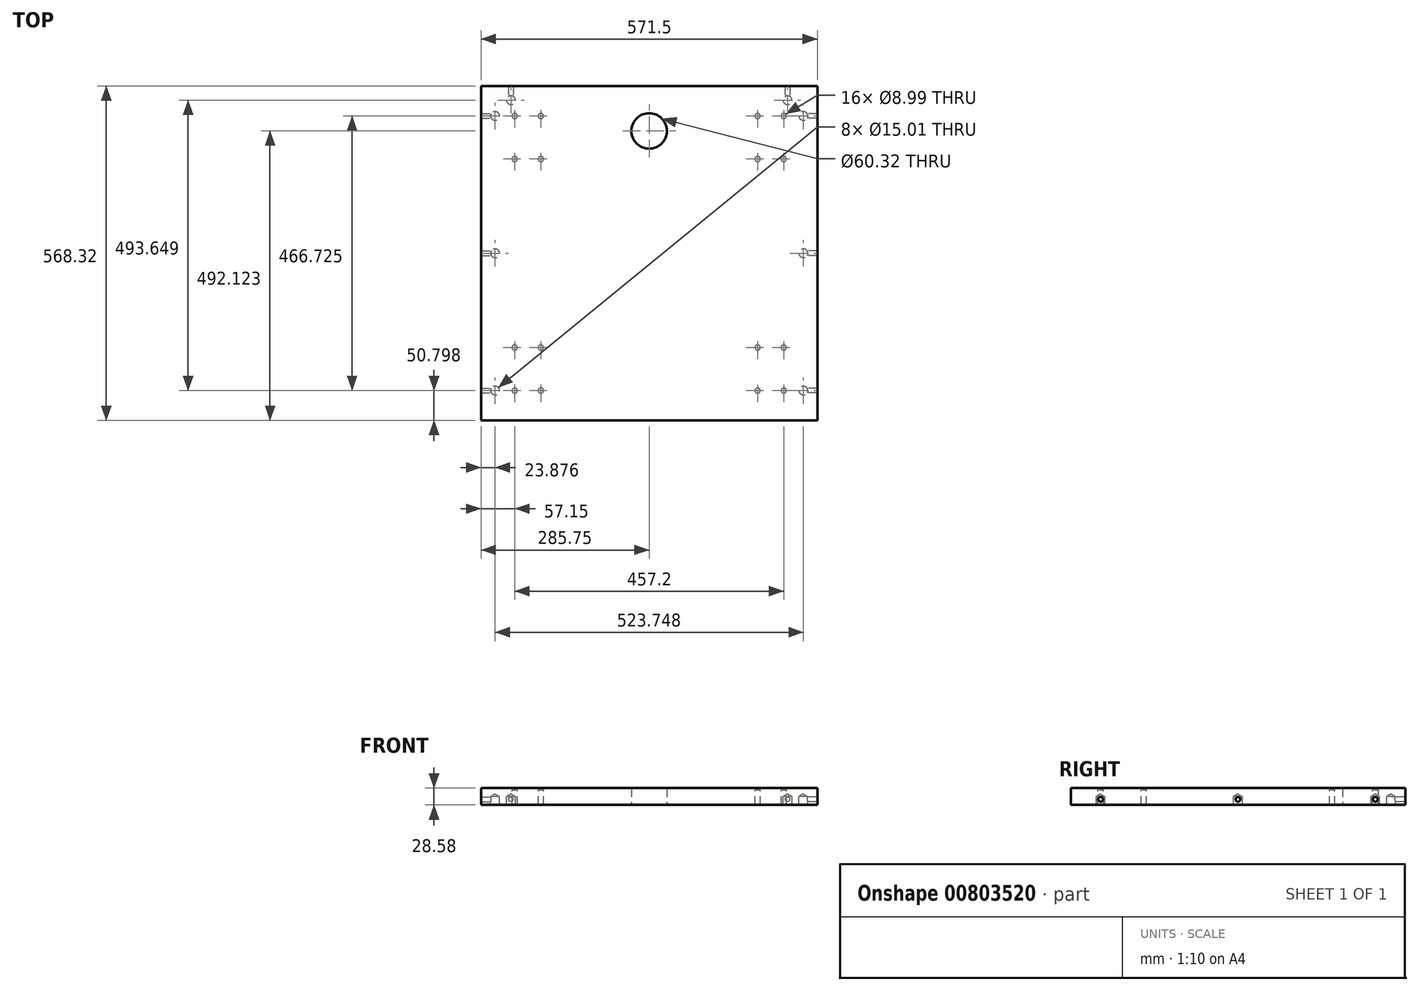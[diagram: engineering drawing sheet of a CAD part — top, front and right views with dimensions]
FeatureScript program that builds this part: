
annotation { "Feature Type Name" : "Feature", "Feature Type Description" : "" }
export const myFeature = defineFeature(function(context is Context, id is Id, definition is map)
    precondition{}
    {
        {
            var Q0;
            Q0=qCreatedBy(makeId("Top.planeOp"),FACE);
            var sketch = newSketch(context, id + "F0", { "sketchPlane" : qUnion([Q0])});
            skLineSegment(sketch, "E0.bottom", {"start": v(285.75, 284.16) * mm, "end": v(-285.75, 284.16) * mm});
            skLineSegment(sketch, "E0.top", {"start": v(285.75, -284.16) * mm, "end": v(-285.75, -284.16) * mm});
            skLineSegment(sketch, "E0.left", {"start": v(285.75, 284.16) * mm, "end": v(285.75, -284.16) * mm});
            skLineSegment(sketch, "E0.right", {"start": v(-285.75, 284.16) * mm, "end": v(-285.75, -284.16) * mm});
            skPoint(sketch, "E0.middle", {"position": v(0, 0) * mm});
            skLineSegment(sketch, "E1", {"start": v(0, 284.16) * mm, "end": v(0, 207.96) * mm});
            skCircle(sketch, "E2", {"center": v(0, 207.96) * mm, "radius": 30.16 * mm});
            skSolve(sketch);
        }
        {
            var Q0;
            Q0=makeQuery(id+"F0.imprint","IMPRINT",FACE,{"disambiguationData":[TD([[makeQuery(id+"F0.imprint","IMPRINT",EDGE,{"derivedFrom":sQuery(id+"F0.wireOp",EDGE,"E0.top")}),-1.0]])]});
            extrude(context, id + "F1", {"entities" : qUnion([Q0]), "depth" : 28.57 * mm, "offsetDistance" : 25.4 * mm});
        }
        {
            var Q0;
            Q0=makeQuery(id+"F1.opExtrude","CAP_FACE",FACE,{"disambiguationData":[OSD([sQuery(id+"F0.wireOp",EDGE,"E0.bottom"),sQuery(id+"F0.wireOp",EDGE,"E0.top"),sQuery(id+"F0.wireOp",EDGE,"E0.left"),sQuery(id+"F0.wireOp",EDGE,"E0.right"),sQuery(id+"F0.wireOp",EDGE,"E2")])],"isStart":true});
            var sketch = newSketch(context, id + "F2", { "sketchPlane" : qUnion([Q0])});
            skLineSegment(sketch, "E3", {"start": v(-285.75, 284.16) * mm, "end": v(-261.87, 284.16) * mm});
            skLineSegment(sketch, "E4", {"start": v(-261.87, 284.16) * mm, "end": v(-261.87, 233.36) * mm});
            skLineSegment(sketch, "E5", {"start": v(-285.75, -284.16) * mm, "end": v(-261.87, -284.16) * mm});
            skLineSegment(sketch, "E6", {"start": v(-261.87, -284.16) * mm, "end": v(-261.87, -233.36) * mm});
            skLineSegment(sketch, "E7", {"start": v(-285.75, 0) * mm, "end": v(-261.87, 0) * mm});
            skLineSegment(sketch, "E8", {"start": v(285.75, 0) * mm, "end": v(261.87, 0) * mm});
            skLineSegment(sketch, "E9", {"start": v(285.75, 284.16) * mm, "end": v(261.87, 284.16) * mm});
            skLineSegment(sketch, "E10", {"start": v(261.87, 284.16) * mm, "end": v(261.87, 233.36) * mm});
            skLineSegment(sketch, "E11", {"start": v(285.75, -284.16) * mm, "end": v(261.87, -284.16) * mm});
            skLineSegment(sketch, "E12", {"start": v(261.87, -284.16) * mm, "end": v(261.87, -233.36) * mm});
            skPoint(sketch, "E13", {"position": v(-261.87, 233.36) * mm});
            skPoint(sketch, "E14", {"position": v(-261.87, 0) * mm});
            skPoint(sketch, "E15", {"position": v(-261.87, -233.36) * mm});
            skPoint(sketch, "E16", {"position": v(261.87, -233.36) * mm});
            skPoint(sketch, "E17", {"position": v(261.87, 0) * mm});
            skPoint(sketch, "E18", {"position": v(261.87, 233.36) * mm});
            skSolve(sketch);
        }
        {
            var Q0;
            Q0=sQuery(id+"F2.wireOp",VERTEX,"E13");
            var Q1;
            Q1=sQuery(id+"F2.wireOp",VERTEX,"E18");
            var Q2;
            Q2=sQuery(id+"F2.wireOp",VERTEX,"E14");
            var Q3;
            Q3=sQuery(id+"F2.wireOp",VERTEX,"E17");
            var Q4;
            Q4=sQuery(id+"F2.wireOp",VERTEX,"E16");
            var Q5;
            Q5=sQuery(id+"F2.wireOp",VERTEX,"E15");
            var Q6;
            Q6=makeQuery(id+"F1.opExtrude","SWEPT_BODY",BODY,{"disambiguationData":[OSD([sQuery(id+"F0.wireOp",EDGE,"E0.bottom"),sQuery(id+"F0.wireOp",EDGE,"E0.top"),sQuery(id+"F0.wireOp",EDGE,"E0.left"),sQuery(id+"F0.wireOp",EDGE,"E0.right"),sQuery(id+"F0.wireOp",EDGE,"E2")])]});
            hole(context, id + "F3", {"style" : HoleStyle.SIMPLE, "endStyle" : HoleEndStyle.BLIND, "holeDiameter" : 15 * mm, "majorDiameter" : 6.35 * mm, "holeDepth" : 14.22 * mm, "isTappedThrough" : true, "tappedDepth" : 12.7 * mm, "tapClearance" : 3, "startFromSketch" : true, "locations" : qUnion([Q0, Q1, Q2, Q3, Q4, Q5]), "scope" : qUnion([Q6])});
        }
        {
            var Q0;
            Q0=makeQuery(id+"F1.opExtrude","SWEPT_FACE",FACE,{"disambiguationData":[OSD([sQuery(id+"F0.wireOp",EDGE,"E0.left")])]});
            var sketch = newSketch(context, id + "F4", { "sketchPlane" : qUnion([Q0])});
            skPoint(sketch, "E19", {"position": v(0, 9.52) * mm});
            skPoint(sketch, "E19.positionSnap0", {"position": v(0, 28.58) * mm});
            skPoint(sketch, "E20", {"position": v(-233.36, 9.53) * mm});
            skPoint(sketch, "E21", {"position": v(233.36, 9.52) * mm});
            skLineSegment(sketch, "E22", {"start": v(-233.36, 9.53) * mm, "end": v(-233.36, 0) * mm});
            skLineSegment(sketch, "E23", {"start": v(-284.16, 0) * mm, "end": v(-233.36, 0) * mm});
            skLineSegment(sketch, "E24", {"start": v(233.36, 9.52) * mm, "end": v(233.36, 0) * mm});
            skLineSegment(sketch, "E25", {"start": v(233.36, 0) * mm, "end": v(284.16, 0) * mm});
            skSolve(sketch);
        }
        {
            var Q0;
            Q0=sQuery(id+"F4.wireOp",VERTEX,"E20");
            var Q1;
            Q1=sQuery(id+"F4.wireOp",VERTEX,"E19");
            var Q2;
            Q2=sQuery(id+"F4.wireOp",VERTEX,"E21");
            var Q3;
            Q3=makeQuery(id+"F1.opExtrude","SWEPT_BODY",BODY,{"disambiguationData":[OSD([sQuery(id+"F0.wireOp",EDGE,"E0.bottom"),sQuery(id+"F0.wireOp",EDGE,"E0.top"),sQuery(id+"F0.wireOp",EDGE,"E0.left"),sQuery(id+"F0.wireOp",EDGE,"E0.right"),sQuery(id+"F0.wireOp",EDGE,"E2")])]});
            hole(context, id + "F5", {"style" : HoleStyle.SIMPLE, "endStyle" : HoleEndStyle.BLIND, "holeDiameter" : 8 * mm, "majorDiameter" : 6.35 * mm, "holeDepth" : 25.4 * mm, "isTappedThrough" : true, "tappedDepth" : 12.7 * mm, "tapClearance" : 3, "startFromSketch" : true, "locations" : qUnion([Q0, Q1, Q2]), "scope" : qUnion([Q3])});
        }
        {
            var Q0;
            Q0=makeQuery(id+"F1.opExtrude","SWEPT_FACE",FACE,{"disambiguationData":[OSD([sQuery(id+"F0.wireOp",EDGE,"E0.right")])]});
            var sketch = newSketch(context, id + "F6", { "sketchPlane" : qUnion([Q0])});
            skPoint(sketch, "E26", {"position": v(-233.36, 9.53) * mm});
            skPoint(sketch, "E27", {"position": v(233.36, 9.52) * mm});
            skLineSegment(sketch, "E28", {"start": v(0, 0) * mm, "end": v(0, 9.53) * mm});
            skPoint(sketch, "E29", {"position": v(0, 9.53) * mm});
            skLineSegment(sketch, "E30", {"start": v(-233.36, 9.53) * mm, "end": v(-233.36, 0) * mm});
            skLineSegment(sketch, "E31", {"start": v(-233.36, 0) * mm, "end": v(-284.16, 0) * mm});
            skLineSegment(sketch, "E32", {"start": v(233.36, 9.52) * mm, "end": v(233.36, 0) * mm});
            skLineSegment(sketch, "E33", {"start": v(233.36, 0) * mm, "end": v(284.16, 0) * mm});
            skSolve(sketch);
        }
        {
            var Q0;
            Q0=sQuery(id+"F6.wireOp",VERTEX,"7JFDCdo1-Y3dr-wsHc-LP2G-7qkS5dpKQL4z.end");
            var Q1;
            Q1=sQuery(id+"F6.wireOp",VERTEX,"E29");
            var Q2;
            Q2=sQuery(id+"F6.wireOp",VERTEX,"E27");
            var Q3;
            Q3=sQuery(id+"F6.wireOp",VERTEX,"E26");
            var Q4;
            Q4=makeQuery(id+"F1.opExtrude","SWEPT_BODY",BODY,{"disambiguationData":[OSD([sQuery(id+"F0.wireOp",EDGE,"E0.bottom"),sQuery(id+"F0.wireOp",EDGE,"E0.top"),sQuery(id+"F0.wireOp",EDGE,"E0.left"),sQuery(id+"F0.wireOp",EDGE,"E0.right"),sQuery(id+"F0.wireOp",EDGE,"E2")])]});
            hole(context, id + "F7", {"style" : HoleStyle.SIMPLE, "endStyle" : HoleEndStyle.BLIND, "holeDiameter" : 8 * mm, "majorDiameter" : 6.35 * mm, "holeDepth" : 25.4 * mm, "isTappedThrough" : true, "tappedDepth" : 12.7 * mm, "tapClearance" : 3, "startFromSketch" : true, "locations" : qUnion([Q0, Q1, Q2, Q3]), "scope" : qUnion([Q4])});
        }
        {
            var Q0;
            Q0=makeQuery(id+"F1.opExtrude","CAP_FACE",FACE,{"disambiguationData":[OSD([sQuery(id+"F0.wireOp",EDGE,"E0.bottom"),sQuery(id+"F0.wireOp",EDGE,"E0.top"),sQuery(id+"F0.wireOp",EDGE,"E0.left"),sQuery(id+"F0.wireOp",EDGE,"E0.right"),sQuery(id+"F0.wireOp",EDGE,"E2")])],"isStart":true});
            var sketch = newSketch(context, id + "F8", { "sketchPlane" : qUnion([Q0])});
            skLineSegment(sketch, "E34", {"start": v(-285.75, 284.16) * mm, "end": v(-228.6, 284.16) * mm});
            skLineSegment(sketch, "E35", {"start": v(-228.6, 284.16) * mm, "end": v(-228.6, 233.36) * mm});
            skLineSegment(sketch, "E36", {"start": v(285.75, 284.16) * mm, "end": v(228.6, 284.16) * mm});
            skLineSegment(sketch, "E37", {"start": v(228.6, 284.16) * mm, "end": v(228.6, 233.36) * mm});
            skLineSegment(sketch, "E38", {"start": v(-285.75, -284.16) * mm, "end": v(-228.6, -284.16) * mm});
            skLineSegment(sketch, "E39", {"start": v(-228.6, -284.16) * mm, "end": v(-228.6, -233.36) * mm});
            skLineSegment(sketch, "E40", {"start": v(285.75, -284.16) * mm, "end": v(228.6, -284.16) * mm});
            skLineSegment(sketch, "E41", {"start": v(228.6, -284.16) * mm, "end": v(228.6, -233.36) * mm});
            skPoint(sketch, "E42", {"position": v(-228.6, 233.36) * mm});
            skPoint(sketch, "E43", {"position": v(228.6, 233.36) * mm});
            skPoint(sketch, "E44", {"position": v(228.6, -233.36) * mm});
            skPoint(sketch, "E45", {"position": v(-228.6, -233.36) * mm});
            skLineSegment(sketch, "E46.bottom", {"start": v(-228.6, 233.36) * mm, "end": v(-184.15, 233.36) * mm});
            skLineSegment(sketch, "E46.top", {"start": v(-228.6, 160.21) * mm, "end": v(-184.15, 160.21) * mm});
            skLineSegment(sketch, "E46.left", {"start": v(-228.6, 233.36) * mm, "end": v(-228.6, 160.21) * mm});
            skLineSegment(sketch, "E46.right", {"start": v(-184.15, 233.36) * mm, "end": v(-184.15, 160.21) * mm});
            skLineSegment(sketch, "E47.bottom", {"start": v(228.6, 233.36) * mm, "end": v(184.15, 233.36) * mm});
            skLineSegment(sketch, "E47.top", {"start": v(228.6, 160.21) * mm, "end": v(184.15, 160.21) * mm});
            skLineSegment(sketch, "E47.left", {"start": v(228.6, 233.36) * mm, "end": v(228.6, 160.21) * mm});
            skLineSegment(sketch, "E47.right", {"start": v(184.15, 233.36) * mm, "end": v(184.15, 160.21) * mm});
            skLineSegment(sketch, "E48.bottom", {"start": v(228.6, -233.36) * mm, "end": v(184.15, -233.36) * mm});
            skLineSegment(sketch, "E48.top", {"start": v(228.6, -160.21) * mm, "end": v(184.15, -160.21) * mm});
            skLineSegment(sketch, "E48.left", {"start": v(228.6, -233.36) * mm, "end": v(228.6, -160.21) * mm});
            skLineSegment(sketch, "E48.right", {"start": v(184.15, -233.36) * mm, "end": v(184.15, -160.21) * mm});
            skLineSegment(sketch, "E49.bottom", {"start": v(-228.6, -233.36) * mm, "end": v(-184.15, -233.36) * mm});
            skLineSegment(sketch, "E49.top", {"start": v(-228.6, -160.21) * mm, "end": v(-184.15, -160.21) * mm});
            skLineSegment(sketch, "E49.left", {"start": v(-228.6, -233.36) * mm, "end": v(-228.6, -160.21) * mm});
            skLineSegment(sketch, "E49.right", {"start": v(-184.15, -233.36) * mm, "end": v(-184.15, -160.21) * mm});
            skPoint(sketch, "E50", {"position": v(-184.15, 233.36) * mm});
            skPoint(sketch, "E51", {"position": v(-228.6, 160.21) * mm});
            skPoint(sketch, "E52", {"position": v(-184.15, 160.21) * mm});
            skPoint(sketch, "E53", {"position": v(184.15, 233.36) * mm});
            skPoint(sketch, "E54", {"position": v(228.6, 160.21) * mm});
            skPoint(sketch, "E55", {"position": v(184.15, 160.21) * mm});
            skPoint(sketch, "E56", {"position": v(184.15, -160.21) * mm});
            skPoint(sketch, "E57", {"position": v(228.6, -160.21) * mm});
            skPoint(sketch, "E58", {"position": v(184.15, -233.36) * mm});
            skPoint(sketch, "E59", {"position": v(-184.15, -233.36) * mm});
            skPoint(sketch, "E60", {"position": v(-184.15, -160.21) * mm});
            skPoint(sketch, "E61", {"position": v(-228.6, -160.21) * mm});
            skSolve(sketch);
        }
        {
            var Q0;
            Q0=sQuery(id+"F8.wireOp",VERTEX,"E45");
            var Q1;
            Q1=sQuery(id+"F8.wireOp",VERTEX,"E59");
            var Q2;
            Q2=sQuery(id+"F8.wireOp",VERTEX,"E60");
            var Q3;
            Q3=sQuery(id+"F8.wireOp",VERTEX,"E61");
            var Q4;
            Q4=sQuery(id+"F8.wireOp",VERTEX,"E51");
            var Q5;
            Q5=sQuery(id+"F8.wireOp",VERTEX,"E42");
            var Q6;
            Q6=sQuery(id+"F8.wireOp",VERTEX,"E50");
            var Q7;
            Q7=sQuery(id+"F8.wireOp",VERTEX,"E52");
            var Q8;
            Q8=sQuery(id+"F8.wireOp",VERTEX,"E53");
            var Q9;
            Q9=sQuery(id+"F8.wireOp",VERTEX,"E43");
            var Q10;
            Q10=sQuery(id+"F8.wireOp",VERTEX,"E54");
            var Q11;
            Q11=sQuery(id+"F8.wireOp",VERTEX,"E55");
            var Q12;
            Q12=sQuery(id+"F8.wireOp",VERTEX,"E56");
            var Q13;
            Q13=sQuery(id+"F8.wireOp",VERTEX,"E57");
            var Q14;
            Q14=sQuery(id+"F8.wireOp",VERTEX,"E44");
            var Q15;
            Q15=sQuery(id+"F8.wireOp",VERTEX,"E58");
            var Q16;
            Q16=makeQuery(id+"F1.opExtrude","SWEPT_BODY",BODY,{"disambiguationData":[OSD([sQuery(id+"F0.wireOp",EDGE,"E0.bottom"),sQuery(id+"F0.wireOp",EDGE,"E0.top"),sQuery(id+"F0.wireOp",EDGE,"E0.left"),sQuery(id+"F0.wireOp",EDGE,"E0.right"),sQuery(id+"F0.wireOp",EDGE,"E2")])]});
            hole(context, id + "F9", {"style" : HoleStyle.SIMPLE, "endStyle" : HoleEndStyle.BLIND, "holeDiameter" : 9 * mm, "majorDiameter" : 6.35 * mm, "holeDepth" : 25.4 * mm, "isTappedThrough" : true, "tappedDepth" : 12.7 * mm, "tapClearance" : 3, "startFromSketch" : true, "locations" : qUnion([Q0, Q1, Q2, Q3, Q4, Q5, Q6, Q7, Q8, Q9, Q10, Q11, Q12, Q13, Q14, Q15]), "scope" : qUnion([Q16])});
        }
        {
            var Q0;
            Q0=makeQuery(id+"F1.opExtrude","CAP_FACE",FACE,{"disambiguationData":[OSD([sQuery(id+"F0.wireOp",EDGE,"E0.bottom"),sQuery(id+"F0.wireOp",EDGE,"E0.top"),sQuery(id+"F0.wireOp",EDGE,"E0.left"),sQuery(id+"F0.wireOp",EDGE,"E0.right"),sQuery(id+"F0.wireOp",EDGE,"E2")])],"isStart":true});
            var sketch = newSketch(context, id + "F10", { "sketchPlane" : qUnion([Q0])});
            skLineSegment(sketch, "E62", {"start": v(-285.75, -284.16) * mm, "end": v(-234.95, -284.16) * mm});
            skLineSegment(sketch, "E63", {"start": v(-234.95, -284.16) * mm, "end": v(-234.95, -260.29) * mm});
            skLineSegment(sketch, "E64", {"start": v(285.75, -284.16) * mm, "end": v(234.95, -284.16) * mm});
            skLineSegment(sketch, "E65", {"start": v(234.95, -284.16) * mm, "end": v(234.95, -260.29) * mm});
            skPoint(sketch, "E66", {"position": v(-234.95, -260.29) * mm});
            skPoint(sketch, "E67", {"position": v(234.95, -260.29) * mm});
            skSolve(sketch);
        }
        {
            var Q0;
            Q0=sQuery(id+"F10.wireOp",VERTEX,"E66");
            var Q1;
            Q1=sQuery(id+"F10.wireOp",VERTEX,"E67");
            var Q2;
            Q2=makeQuery(id+"F1.opExtrude","SWEPT_BODY",BODY,{"disambiguationData":[OSD([sQuery(id+"F0.wireOp",EDGE,"E0.bottom"),sQuery(id+"F0.wireOp",EDGE,"E0.top"),sQuery(id+"F0.wireOp",EDGE,"E0.left"),sQuery(id+"F0.wireOp",EDGE,"E0.right"),sQuery(id+"F0.wireOp",EDGE,"E2")])]});
            hole(context, id + "F11", {"style" : HoleStyle.SIMPLE, "endStyle" : HoleEndStyle.BLIND, "holeDiameter" : 15 * mm, "majorDiameter" : 6.35 * mm, "holeDepth" : 14.22 * mm, "isTappedThrough" : true, "tappedDepth" : 12.7 * mm, "tapClearance" : 3, "startFromSketch" : true, "locations" : qUnion([Q0, Q1]), "scope" : qUnion([Q2])});
        }
        {
            var Q0;
            Q0=makeQuery(id+"F1.opExtrude","SWEPT_FACE",FACE,{"disambiguationData":[OSD([sQuery(id+"F0.wireOp",EDGE,"E0.bottom")])]});
            var sketch = newSketch(context, id + "F12", { "sketchPlane" : qUnion([Q0])});
            skLineSegment(sketch, "E68", {"start": v(-285.75, 0) * mm, "end": v(-285.75, 9.53) * mm});
            skLineSegment(sketch, "E69", {"start": v(-285.75, 9.53) * mm, "end": v(-234.95, 9.53) * mm});
            skLineSegment(sketch, "E70", {"start": v(285.75, 0) * mm, "end": v(285.75, 9.53) * mm});
            skLineSegment(sketch, "E71", {"start": v(285.75, 9.53) * mm, "end": v(234.95, 9.53) * mm});
            skPoint(sketch, "E72", {"position": v(-234.95, 9.53) * mm});
            skPoint(sketch, "E73", {"position": v(234.95, 9.53) * mm});
            skSolve(sketch);
        }
        {
            var Q0;
            Q0=sQuery(id+"F12.wireOp",VERTEX,"E69.end");
            var Q1;
            Q1=sQuery(id+"F12.wireOp",VERTEX,"E73");
            var Q2;
            Q2=makeQuery(id+"F1.opExtrude","SWEPT_BODY",BODY,{"disambiguationData":[OSD([sQuery(id+"F0.wireOp",EDGE,"E0.bottom"),sQuery(id+"F0.wireOp",EDGE,"E0.top"),sQuery(id+"F0.wireOp",EDGE,"E0.left"),sQuery(id+"F0.wireOp",EDGE,"E0.right"),sQuery(id+"F0.wireOp",EDGE,"E2")])]});
            hole(context, id + "F13", {"style" : HoleStyle.SIMPLE, "endStyle" : HoleEndStyle.BLIND, "holeDiameter" : 8 * mm, "majorDiameter" : 6.35 * mm, "holeDepth" : 25.4 * mm, "isTappedThrough" : true, "tappedDepth" : 12.7 * mm, "tapClearance" : 3, "startFromSketch" : true, "locations" : qUnion([Q0, Q1]), "scope" : qUnion([Q2])});
        }
    });
